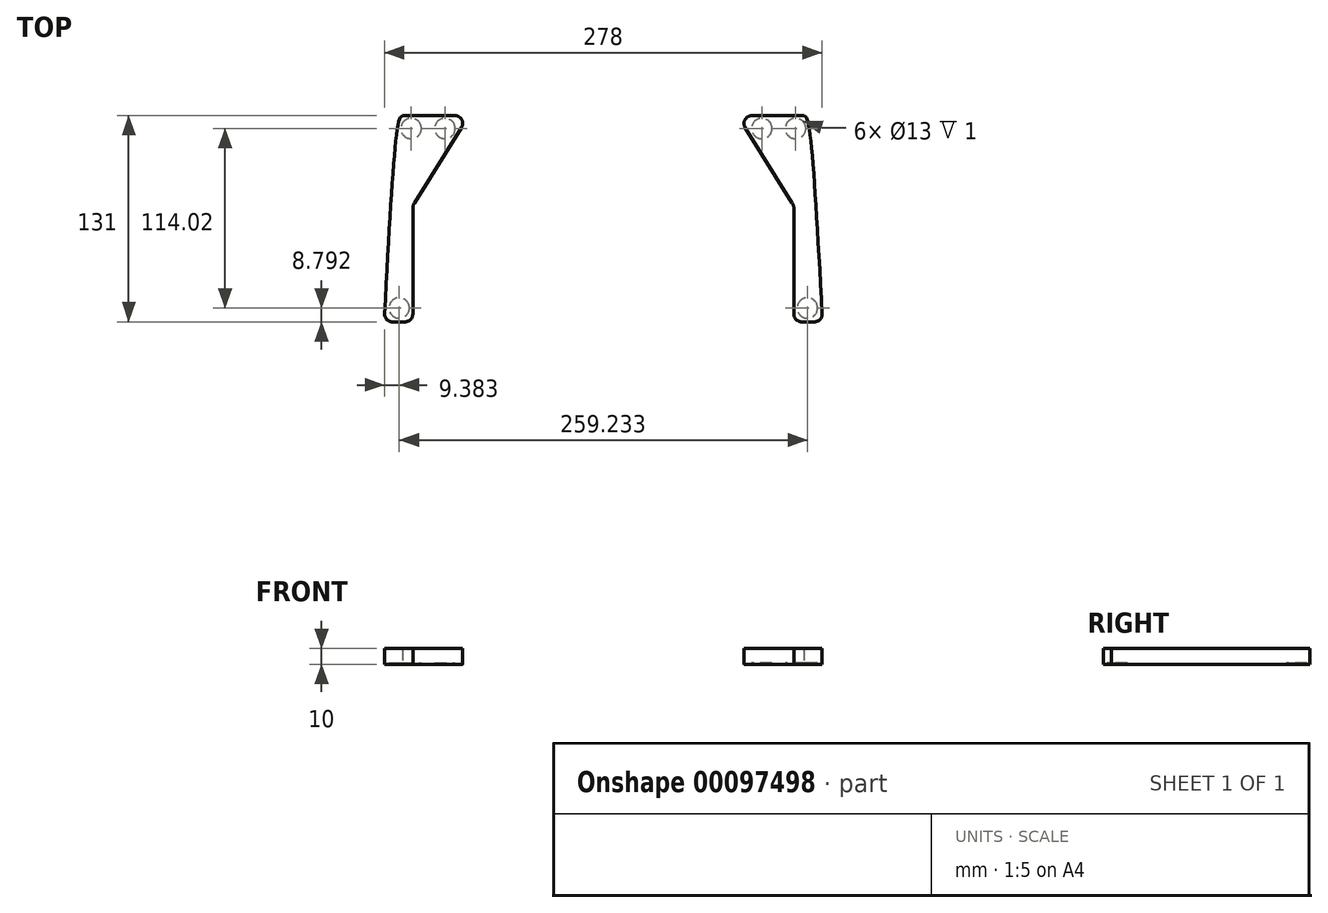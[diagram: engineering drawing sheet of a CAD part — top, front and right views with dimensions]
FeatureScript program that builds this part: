
annotation { "Feature Type Name" : "Feature", "Feature Type Description" : "" }
export const myFeature = defineFeature(function(context is Context, id is Id, definition is map)
    precondition{}
    {
        {
            var Q0;
            Q0=qCreatedBy(makeId("Top.planeOp"),FACE);
            var sketch = newSketch(context, id + "F0", { "sketchPlane" : qUnion([Q0])});
            skLineSegment(sketch, "E0.bottom", {"start": v(-116, 0) * mm, "end": v(116, 0) * mm, "construction": true});
            skLineSegment(sketch, "E0.left", {"start": v(-121, -5) * mm, "end": v(-121, -58.9) * mm, "construction": true});
            skLineSegment(sketch, "E0.right", {"start": v(121, -5) * mm, "end": v(121, -58.9) * mm, "construction": true});
            skPoint(sketch, "E1.visualSharp", {"position": v(-121, 0) * mm});
            skArc(sketch, "E1.filletArc", {"start": v(-116, 0) * mm, "mid": v(-119.54, -1.46) * mm, "end": v(-121, -5) * mm, "construction": true});
            skPoint(sketch, "E2.visualSharp", {"position": v(121, 0) * mm});
            skArc(sketch, "E2.filletArc", {"start": v(121, -5) * mm, "mid": v(119.54, -1.46) * mm, "end": v(116, 0) * mm, "construction": true});
            skPoint(sketch, "E3", {"position": v(0, 0) * mm});
            skSolve(sketch);
        }
        {
            var Q0;
            Q0=qCreatedBy(makeId("Top.planeOp"),FACE);
            var sketch = newSketch(context, id + "F1", { "sketchPlane" : qUnion([Q0])});
            skLineSegment(sketch, "E4", {"start": v(-127.5, 60) * mm, "end": v(127.5, 60) * mm, "construction": true});
            skPoint(sketch, "E5", {"position": v(0, 60) * mm});
            skFitSpline(sketch, "E6", {"points": [v(-127.5, 60) * mm, v(-129.6, 57.32) * mm, v(-139, -71) * mm], "startDerivative": vector(-12.2, -8.72) * mm, "endDerivative": vector(-8.53, -123.24) * mm, "construction": true});
            skLineSegment(sketch, "E7", {"start": v(0, 60) * mm, "end": v(0, -64.89) * mm, "construction": true});
            skFitSpline(sketch, "E8.MirrorCS", {"points": [v(127.5, 60) * mm, v(129.6, 57.32) * mm, v(139, -71) * mm], "startDerivative": vector(12.2, -8.72) * mm, "endDerivative": vector(8.53, -123.24) * mm, "construction": true});
            skLineSegment(sketch, "E9", {"start": v(-139, -71) * mm, "end": v(139, -71) * mm, "construction": true});
            skLineSegment(sketch, "E10", {"start": v(-129.6, 57.32) * mm, "end": v(-99.54, 57.32) * mm, "construction": true});
            skLineSegment(sketch, "E11", {"start": v(-127.5, 60) * mm, "end": v(-127.5, 20.17) * mm, "construction": true});
            skPoint(sketch, "E12", {"position": v(-127.5, 57.32) * mm});
            skLineSegment(sketch, "E13", {"start": v(0, 0) * mm, "end": v(190.06, 0) * mm, "construction": true});
            skLineSegment(sketch, "E14", {"start": v(121, -10.82) * mm, "end": v(121, 17.33) * mm, "construction": true});
            skPoint(sketch, "E15", {"position": v(135.17, 0) * mm});
            skCircle(sketch, "E16", {"center": v(-117.5, 43) * mm, "radius": 6.5 * mm, "construction": true});
            skCircle(sketch, "E17", {"center": v(-122, -61) * mm, "radius": 6.5 * mm, "construction": true});
            skSolve(sketch);
        }
        {
            var Q0;
            Q0=qCreatedBy(makeId("Top.planeOp"),FACE);
            var sketch = newSketch(context, id + "F2", { "sketchPlane" : qUnion([Q0])});
            skLineSegment(sketch, "E18.top", {"start": v(-134, -71) * mm, "end": v(-126, -71) * mm});
            skLineSegment(sketch, "E18.right", {"start": v(-121, 0.87) * mm, "end": v(-121, -66) * mm});
            skLineSegment(sketch, "E19", {"start": v(-139, -45.67) * mm, "end": v(-139, -91.08) * mm, "construction": true});
            skPoint(sketch, "E20.visualSharp", {"position": v(-147, -71) * mm});
            skArc(sketch, "E20.filletArc", {"start": v(-139, -66) * mm, "mid": v(-137.54, -69.54) * mm, "end": v(-134, -71) * mm});
            skPoint(sketch, "E21.visualSharp", {"position": v(-121, -71) * mm});
            skArc(sketch, "E21.filletArc", {"start": v(-126, -71) * mm, "mid": v(-122.46, -69.54) * mm, "end": v(-121, -66) * mm});
            skLineSegment(sketch, "E22", {"start": v(-123, 60) * mm, "end": v(-127.5, 60) * mm});
            skFitSpline(sketch, "E23", {"points": [v(-127.5, 60) * mm, v(-129.6, 57.32) * mm, v(-139, -66) * mm], "startDerivative": vector(-21.73, -12.12) * mm, "endDerivative": vector(-12.37, -223.95) * mm});
            skPoint(sketch, "E24.visualSharp", {"position": v(-121, 60) * mm});
            skLineSegment(sketch, "E24.filletArc", {"start": v(-123, 60) * mm, "end": v(-123, 60) * mm});
            skLineSegment(sketch, "E25", {"start": v(-119.94, 4.58) * mm, "end": v(-90.09, 52.35) * mm});
            skLineSegment(sketch, "E26", {"start": v(-94.33, 60) * mm, "end": v(-123, 60) * mm});
            skPoint(sketch, "E27.visualSharp", {"position": v(-85.3, 60) * mm});
            skArc(sketch, "E27.filletArc", {"start": v(-90.09, 52.35) * mm, "mid": v(-89.96, 57.42) * mm, "end": v(-94.33, 60) * mm});
            skPoint(sketch, "E28.visualSharp", {"position": v(-121, 2.88) * mm});
            skArc(sketch, "E28.filletArc", {"start": v(-119.94, 4.58) * mm, "mid": v(-120.73, 2.8) * mm, "end": v(-121, 0.87) * mm});
            skSolve(sketch);
        }
        {
            var Q0;
            Q0=makeQuery(id+"F2.imprint","IMPRINT",FACE,{"disambiguationData":[TD([[makeQuery(id+"F2.imprint","IMPRINT",EDGE,{"derivedFrom":sQuery(id+"F2.wireOp",EDGE,"E18.top")}),1.0]])]});
            extrude(context, id + "F3", {"entities" : qUnion([Q0]), "depth" : 10 * mm});
        }
        {
            var Q0;
            Q0=makeQuery(id+"F3.opExtrude","CAP_FACE",FACE,{"disambiguationData":[OSD([sQuery(id+"F2.wireOp",EDGE,"E18.top"),sQuery(id+"F2.wireOp",EDGE,"E18.right"),sQuery(id+"F2.wireOp",EDGE,"E20.filletArc"),sQuery(id+"F2.wireOp",EDGE,"E21.filletArc"),sQuery(id+"F2.wireOp",EDGE,"E22"),sQuery(id+"F2.wireOp",EDGE,"E23"),sQuery(id+"F2.wireOp",EDGE,"E25"),sQuery(id+"F2.wireOp",EDGE,"E26"),sQuery(id+"F2.wireOp",EDGE,"E27.filletArc"),sQuery(id+"F2.wireOp",EDGE,"E28.filletArc")])],"isStart":false});
            var sketch = newSketch(context, id + "F4", { "sketchPlane" : qUnion([Q0])});
            skCircle(sketch, "E29", {"center": v(-117.5, 43) * mm, "radius": 6.5 * mm});
            skCircle(sketch, "E30", {"center": v(-122, -61) * mm, "radius": 6.5 * mm});
            skSolve(sketch);
        }
        {
            var Q0;
            Q0=makeQuery(id+"F3.opExtrude","CAP_FACE",FACE,{"disambiguationData":[OSD([sQuery(id+"F2.wireOp",EDGE,"E18.top"),sQuery(id+"F2.wireOp",EDGE,"E18.right"),sQuery(id+"F2.wireOp",EDGE,"E20.filletArc"),sQuery(id+"F2.wireOp",EDGE,"E21.filletArc"),sQuery(id+"F2.wireOp",EDGE,"E22"),sQuery(id+"F2.wireOp",EDGE,"E23"),sQuery(id+"F2.wireOp",EDGE,"E25"),sQuery(id+"F2.wireOp",EDGE,"E26"),sQuery(id+"F2.wireOp",EDGE,"E27.filletArc"),sQuery(id+"F2.wireOp",EDGE,"E28.filletArc")])],"isStart":true});
            var sketch = newSketch(context, id + "F5", { "sketchPlane" : qUnion([Q0])});
            skCircle(sketch, "E31", {"center": v(-129.62, 62.2) * mm, "radius": 6.5 * mm});
            skCircle(sketch, "E32", {"center": v(-100.62, -51.81) * mm, "radius": 6.5 * mm});
            skCircle(sketch, "E33", {"center": v(-122.09, -51.81) * mm, "radius": 6.5 * mm});
            skLineSegment(sketch, "E34", {"start": v(-100.62, -51.81) * mm, "end": v(-140.76, -51.81) * mm, "construction": true});
            skSolve(sketch);
        }
        {
            var Q0;
            Q0 = qSketchRegion(id + "F5", true);
            extrude(context, id + "F6", {"entities" : qUnion([Q0]), "operationType" : NewBodyOperationType.REMOVE, "oppositeDirection" : true, "depth" : 1 * mm});
        }
        {
            var Q0;
            Q0=makeQuery(id+"F3.opExtrude","SWEPT_BODY",BODY,{"disambiguationData":[OSD([sQuery(id+"F2.wireOp",EDGE,"E18.top"),sQuery(id+"F2.wireOp",EDGE,"E18.right"),sQuery(id+"F2.wireOp",EDGE,"E20.filletArc"),sQuery(id+"F2.wireOp",EDGE,"E21.filletArc"),sQuery(id+"F2.wireOp",EDGE,"E22"),sQuery(id+"F2.wireOp",EDGE,"E23"),sQuery(id+"F2.wireOp",EDGE,"E25"),sQuery(id+"F2.wireOp",EDGE,"E26"),sQuery(id+"F2.wireOp",EDGE,"E27.filletArc"),sQuery(id+"F2.wireOp",EDGE,"E28.filletArc")])]});
            var Q1;
            Q1=qCreatedBy(makeId("Right.planeOp"),FACE);
            mirror(context, id + "F7", {"entities" : qUnion([Q0]), "mirrorPlane" : qUnion([Q1])});
        }
    });
